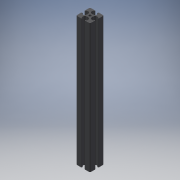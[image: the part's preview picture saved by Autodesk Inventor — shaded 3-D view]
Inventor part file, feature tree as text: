
AUTODESK INVENTOR PART (.ipt)
format: ipt  version: 2016 (Build 200138000, 138)  size: 171,520 bytes
history: native  units: mm
features: extrude x1, sketch x1
ambient origin geometry x8: Origin, YZ Plane, XZ Plane, XY Plane, X Axis, Y Axis, Z Axis, Center Point
bodies: Solid1 (feature_tree)
feature tree (2):
  extrude  "Extrusion1"  [1 undecoded]
  sketch  "Sketch_1"  dims[d0=140.0mm d1=0.0mm]
note: 1 required parameter value undecoded (feature->parameter linkage not recoverable at this tier; creation-order binding heuristic only, values carry confidence <= 0.55)
